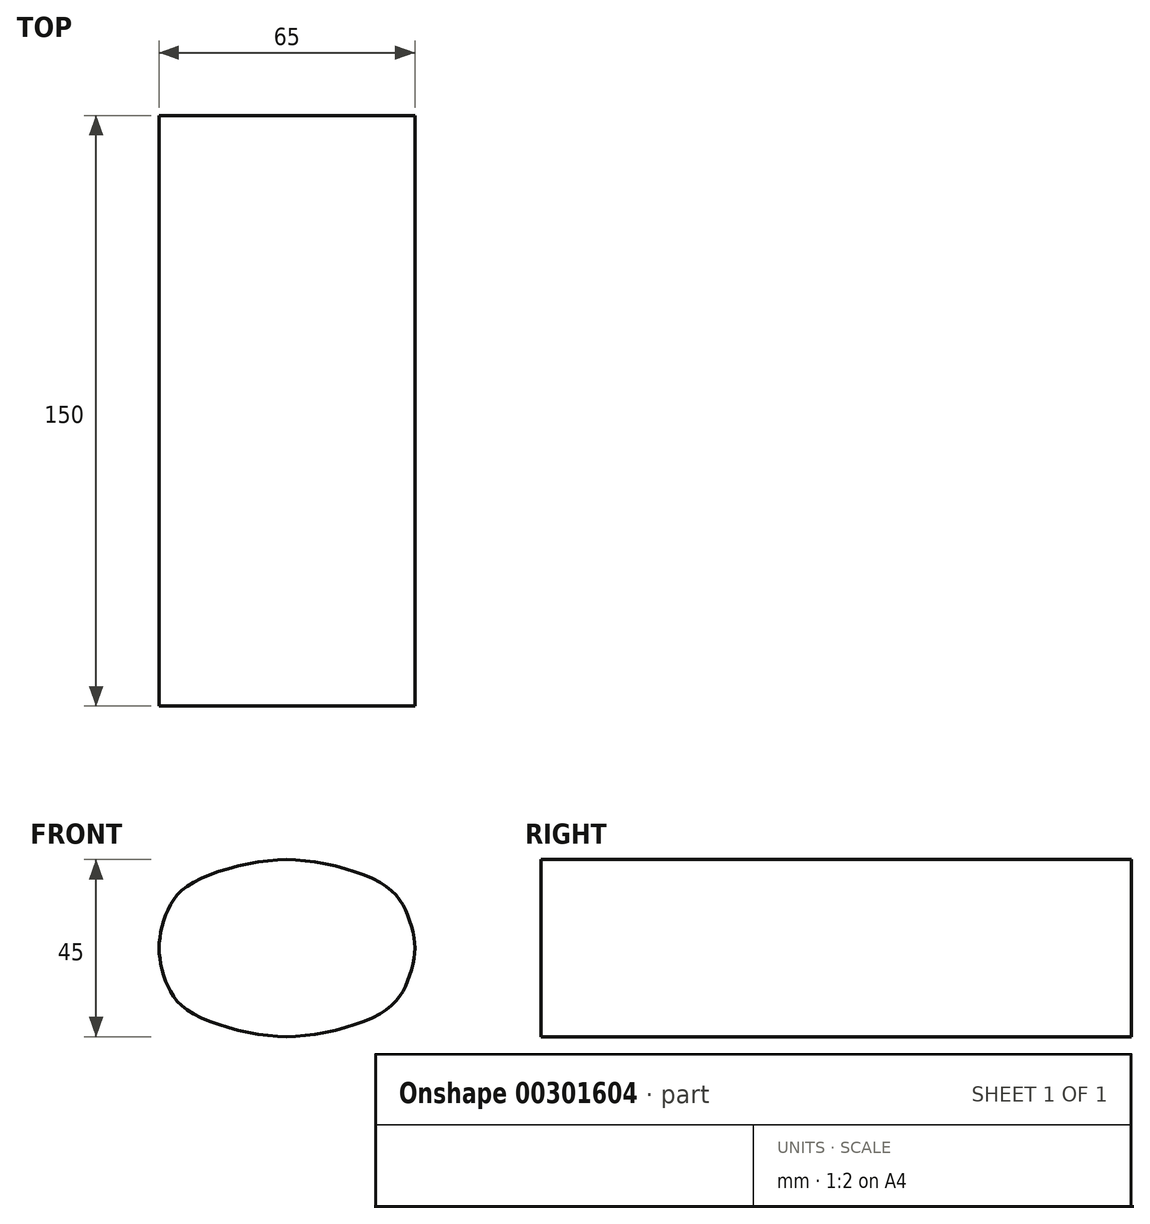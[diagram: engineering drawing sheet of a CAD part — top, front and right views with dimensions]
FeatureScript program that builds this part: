
annotation { "Feature Type Name" : "Feature", "Feature Type Description" : "" }
export const myFeature = defineFeature(function(context is Context, id is Id, definition is map)
    precondition{}
    {
        {
            var Q0;
            Q0=qCreatedBy(makeId("Front.planeOp"),FACE);
            var sketch = newSketch(context, id + "F0", { "sketchPlane" : qUnion([Q0])});
            skLineSegment(sketch, "E0", {"start": v(0, 40.3) * mm, "end": v(0, 0) * mm, "construction": true});
            skLineSegment(sketch, "E1", {"start": v(0, 0) * mm, "end": v(44.4, 0) * mm, "construction": true});
            skFitSpline(sketch, "E2", {"points": [v(0, 22.5) * mm, v(24.2, 16.39) * mm, v(30.7, 8.5) * mm, v(32.58, 0) * mm], "startDerivative": vector(50.82, 0) * mm, "endDerivative": vector(0, -28.17) * mm});
            skFitSpline(sketch, "E3.MirrorCS", {"points": [v(0, -22.5) * mm, v(24.2, -16.39) * mm, v(30.7, -8.5) * mm, v(32.58, 0) * mm], "startDerivative": vector(50.82, 0) * mm, "endDerivative": vector(0, 28.17) * mm});
            skFitSpline(sketch, "E4.MirrorCS", {"points": [v(0, -22.5) * mm, v(-24.2, -16.39) * mm, v(-30.7, -8.5) * mm, v(-32.42, 0) * mm], "startDerivative": vector(-50.88, 0) * mm, "endDerivative": vector(0, 28.19) * mm});
            skFitSpline(sketch, "E5.MirrorCS", {"points": [v(0, 22.5) * mm, v(-24.2, 16.39) * mm, v(-30.7, 8.5) * mm, v(-32.42, 0) * mm], "startDerivative": vector(-50.88, 0) * mm, "endDerivative": vector(0, -28.19) * mm});
            skSolve(sketch);
        }
        {
            var Q0;
            Q0=qSketchRegion(id+"F0",true);
            extrude(context, id + "F1", {"entities" : qUnion([Q0]), "depth" : 150 * mm});
        }
    });
